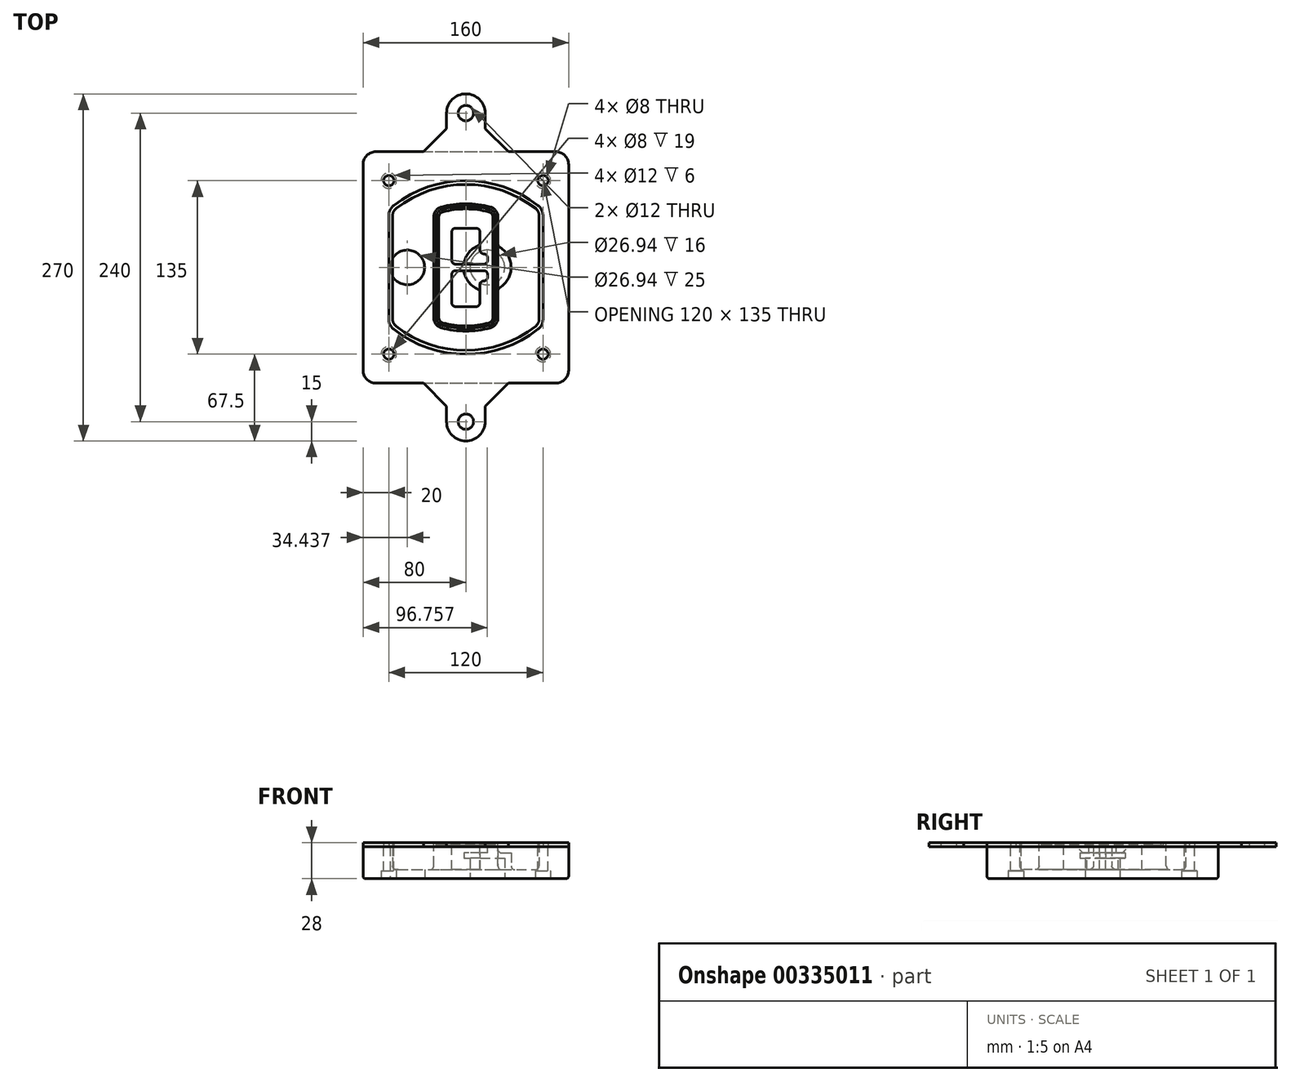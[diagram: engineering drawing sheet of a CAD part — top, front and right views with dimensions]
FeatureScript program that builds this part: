
annotation { "Feature Type Name" : "Feature", "Feature Type Description" : "" }
export const myFeature = defineFeature(function(context is Context, id is Id, definition is map)
    precondition{}
    {
        {
            var Q0;
            Q0=qCreatedBy(makeId("Top.planeOp"),FACE);
            var sketch = newSketch(context, id + "F0", { "sketchPlane" : qUnion([Q0])});
            skPoint(sketch, "E0.rect.middle", {"position": v(0, 0) * mm});
            skLineSegment(sketch, "E1.bottom", {"start": v(-70, -90) * mm, "end": v(70, -90) * mm});
            skLineSegment(sketch, "E1.top", {"start": v(-70, 90) * mm, "end": v(70, 90) * mm});
            skLineSegment(sketch, "E1.left", {"start": v(-80, -80) * mm, "end": v(-80, 80) * mm});
            skLineSegment(sketch, "E1.right", {"start": v(80, -80) * mm, "end": v(80, 80) * mm});
            skLineSegment(sketch, "E2", {"start": v(-80, 90) * mm, "end": v(80, -90) * mm, "construction": true});
            skLineSegment(sketch, "E3", {"start": v(80, 90) * mm, "end": v(-80, -90) * mm, "construction": true});
            skCircle(sketch, "E4", {"center": v(-60, 67.5) * mm, "radius": 4 * mm});
            skCircle(sketch, "E5", {"center": v(60, 67.5) * mm, "radius": 4 * mm});
            skCircle(sketch, "E6", {"center": v(60, -67.5) * mm, "radius": 4 * mm});
            skCircle(sketch, "E7", {"center": v(-60, -67.5) * mm, "radius": 4 * mm});
            skLineSegment(sketch, "E8", {"start": v(-60, 67.5) * mm, "end": v(60, 67.5) * mm, "construction": true});
            skLineSegment(sketch, "E9", {"start": v(60, 67.5) * mm, "end": v(60, -67.5) * mm, "construction": true});
            skLineSegment(sketch, "E10", {"start": v(60, -67.5) * mm, "end": v(-60, -67.5) * mm, "construction": true});
            skLineSegment(sketch, "E11", {"start": v(-60, -67.5) * mm, "end": v(-60, 67.5) * mm, "construction": true});
            skLineSegment(sketch, "E12", {"start": v(-60, 40.3) * mm, "end": v(-60, -40.3) * mm});
            skLineSegment(sketch, "E13", {"start": v(60, 40.3) * mm, "end": v(60, -40.3) * mm});
            skArc(sketch, "E14", {"start": v(56.15, 48.18) * mm, "mid": v(0, 67.5) * mm, "end": v(-56.15, 48.18) * mm});
            skArc(sketch, "E15", {"start": v(-56.15, -48.18) * mm, "mid": v(0, -67.5) * mm, "end": v(56.15, -48.18) * mm});
            skLineSegment(sketch, "E16", {"start": v(-60, 0) * mm, "end": v(60, 0) * mm, "construction": true});
            skPoint(sketch, "E17.visualSharp", {"position": v(-60, -45) * mm});
            skArc(sketch, "E17.filletArc", {"start": v(-60, -40.3) * mm, "mid": v(-58.99, -44.68) * mm, "end": v(-56.15, -48.18) * mm});
            skPoint(sketch, "E18.visualSharp", {"position": v(-60, 45) * mm});
            skArc(sketch, "E18.filletArc", {"start": v(-56.15, 48.18) * mm, "mid": v(-58.99, 44.68) * mm, "end": v(-60, 40.3) * mm});
            skPoint(sketch, "E19.visualSharp", {"position": v(60, 45) * mm});
            skArc(sketch, "E19.filletArc", {"start": v(60, 40.3) * mm, "mid": v(58.99, 44.68) * mm, "end": v(56.15, 48.18) * mm});
            skPoint(sketch, "E20.visualSharp", {"position": v(60, -45) * mm});
            skArc(sketch, "E20.filletArc", {"start": v(56.15, -48.18) * mm, "mid": v(58.99, -44.68) * mm, "end": v(60, -40.3) * mm});
            skPoint(sketch, "E21.visualSharp", {"position": v(-80, 90) * mm});
            skArc(sketch, "E21.filletArc", {"start": v(-70, 90) * mm, "mid": v(-77.07, 87.07) * mm, "end": v(-80, 80) * mm});
            skPoint(sketch, "E22.visualSharp", {"position": v(80, 90) * mm});
            skArc(sketch, "E22.filletArc", {"start": v(80, 80) * mm, "mid": v(77.07, 87.07) * mm, "end": v(70, 90) * mm});
            skPoint(sketch, "E23.visualSharp", {"position": v(80, -90) * mm});
            skArc(sketch, "E23.filletArc", {"start": v(70, -90) * mm, "mid": v(77.07, -87.07) * mm, "end": v(80, -80) * mm});
            skPoint(sketch, "E24.visualSharp", {"position": v(-80, -90) * mm});
            skArc(sketch, "E24.filletArc", {"start": v(-80, -80) * mm, "mid": v(-77.07, -87.07) * mm, "end": v(-70, -90) * mm});
            skArc(sketch, "E25.0", {"start": v(57, 40.3) * mm, "mid": v(56.3, 43.36) * mm, "end": v(54.3, 45.81) * mm});
            skLineSegment(sketch, "E25.1", {"start": v(57, 40.3) * mm, "end": v(57, -40.3) * mm});
            skArc(sketch, "E25.2", {"start": v(54.3, -45.81) * mm, "mid": v(56.3, -43.36) * mm, "end": v(57, -40.3) * mm});
            skArc(sketch, "E25.3", {"start": v(-54.3, -45.81) * mm, "mid": v(0, -64.5) * mm, "end": v(54.3, -45.81) * mm});
            skArc(sketch, "E25.4", {"start": v(-57, -40.3) * mm, "mid": v(-56.3, -43.36) * mm, "end": v(-54.3, -45.81) * mm});
            skArc(sketch, "E25.5", {"start": v(54.3, 45.81) * mm, "mid": v(0, 64.5) * mm, "end": v(-54.3, 45.81) * mm});
            skLineSegment(sketch, "E25.6", {"start": v(-57, 40.3) * mm, "end": v(-57, -40.3) * mm});
            skArc(sketch, "E25.7", {"start": v(-54.3, 45.81) * mm, "mid": v(-56.3, 43.36) * mm, "end": v(-57, 40.3) * mm});
            skArc(sketch, "E26.0", {"start": v(-58.62, 51.33) * mm, "mid": v(-62.58, 46.43) * mm, "end": v(-64, 40.3) * mm});
            skArc(sketch, "E26.1", {"start": v(58.62, 51.33) * mm, "mid": v(0, 71.5) * mm, "end": v(-58.62, 51.33) * mm});
            skArc(sketch, "E26.2", {"start": v(64, 40.3) * mm, "mid": v(62.58, 46.43) * mm, "end": v(58.62, 51.33) * mm});
            skLineSegment(sketch, "E26.3", {"start": v(64, 40.3) * mm, "end": v(64, -40.3) * mm});
            skArc(sketch, "E26.4", {"start": v(58.62, -51.33) * mm, "mid": v(62.58, -46.43) * mm, "end": v(64, -40.3) * mm});
            skLineSegment(sketch, "E26.5", {"start": v(-64, 40.3) * mm, "end": v(-64, -40.3) * mm});
            skArc(sketch, "E26.6", {"start": v(-58.62, -51.33) * mm, "mid": v(0, -71.5) * mm, "end": v(58.62, -51.33) * mm});
            skArc(sketch, "E26.7", {"start": v(-64, -40.3) * mm, "mid": v(-62.58, -46.43) * mm, "end": v(-58.62, -51.33) * mm});
            skSolve(sketch);
        }
        {
            var Q0;
            Q0=makeQuery(id+"F0.imprint","IMPRINT",FACE,{"disambiguationData":[TD([[makeQuery(id+"F0.imprint","IMPRINT",EDGE,{"derivedFrom":sQuery(id+"F0.wireOp",EDGE,"E1.bottom")}),1.0]])]});
            var Q1;
            Q1=makeQuery(id+"F0.imprint","IMPRINT",FACE,{"disambiguationData":[TD([[makeQuery(id+"F0.imprint","IMPRINT",EDGE,{"derivedFrom":sQuery(id+"F0.wireOp",EDGE,"E12")}),1.0]])]});
            var Q2;
            Q2=makeQuery(id+"F0.imprint","IMPRINT",FACE,{"disambiguationData":[TD([[makeQuery(id+"F0.imprint","IMPRINT",EDGE,{"derivedFrom":sQuery(id+"F0.wireOp",EDGE,"E25.0")}),1.0]])]});
            var Q3;
            Q3=makeQuery(id+"F0.imprint","IMPRINT",FACE,{"disambiguationData":[TD([[makeQuery(id+"F0.imprint","IMPRINT",EDGE,{"derivedFrom":sQuery(id+"F0.wireOp",EDGE,"E12")}),-1.0]])]});
            extrude(context, id + "F1", {"entities" : qUnion([Q0, Q1, Q2, Q3]), "oppositeDirection" : true, "depth" : 25 * mm});
        }
        {
            var Q0;
            Q0=makeQuery(id+"F0.imprint","IMPRINT",FACE,{"disambiguationData":[TD([[makeQuery(id+"F0.imprint","IMPRINT",EDGE,{"derivedFrom":sQuery(id+"F0.wireOp",EDGE,"E12")}),1.0]])]});
            extrude(context, id + "F2", {"entities" : qUnion([Q0]), "operationType" : NewBodyOperationType.ADD, "depth" : 3 * mm});
        }
        {
            var Q0;
            Q0=makeQuery(id+"F0.imprint","IMPRINT",FACE,{"disambiguationData":[TD([[makeQuery(id+"F0.imprint","IMPRINT",EDGE,{"derivedFrom":sQuery(id+"F0.wireOp",EDGE,"E25.0")}),1.0]])]});
            extrude(context, id + "F3", {"entities" : qUnion([Q0]), "operationType" : NewBodyOperationType.REMOVE, "oppositeDirection" : true, "depth" : 18 * mm});
        }
        {
            var Q0;
            Q0=makeQuery(id+"F2.opExtrude","CAP_FACE",FACE,{"disambiguationData":[OSD([sQuery(id+"F0.wireOp",EDGE,"E12"),sQuery(id+"F0.wireOp",EDGE,"E13"),sQuery(id+"F0.wireOp",EDGE,"E14"),sQuery(id+"F0.wireOp",EDGE,"E15"),sQuery(id+"F0.wireOp",EDGE,"E17.filletArc"),sQuery(id+"F0.wireOp",EDGE,"E18.filletArc"),sQuery(id+"F0.wireOp",EDGE,"E19.filletArc"),sQuery(id+"F0.wireOp",EDGE,"E20.filletArc"),sQuery(id+"F0.wireOp",EDGE,"E25.0"),sQuery(id+"F0.wireOp",EDGE,"E25.1"),sQuery(id+"F0.wireOp",EDGE,"E25.2"),sQuery(id+"F0.wireOp",EDGE,"E25.3"),sQuery(id+"F0.wireOp",EDGE,"E25.4"),sQuery(id+"F0.wireOp",EDGE,"E25.5"),sQuery(id+"F0.wireOp",EDGE,"E25.6"),sQuery(id+"F0.wireOp",EDGE,"E25.7")])],"isStart":false});
            var sketch = newSketch(context, id + "F4", { "sketchPlane" : qUnion([Q0])});
            skArc(sketch, "E27.0", {"start": v(-19.08, -46.97) * mm, "mid": v(0, -49.5) * mm, "end": v(19.08, -46.97) * mm});
            skArc(sketch, "E28.0", {"start": v(19.08, 46.97) * mm, "mid": v(0, 49.5) * mm, "end": v(-19.08, 46.97) * mm});
            skLineSegment(sketch, "E29", {"start": v(-25, 39.25) * mm, "end": v(-25, -39.25) * mm});
            skLineSegment(sketch, "E30", {"start": v(25, 39.25) * mm, "end": v(25, -39.25) * mm});
            skLineSegment(sketch, "E31", {"start": v(-25, 45.1) * mm, "end": v(25, 45.1) * mm, "construction": true});
            skLineSegment(sketch, "E32", {"start": v(-25, -45.1) * mm, "end": v(25, -45.1) * mm, "construction": true});
            skPoint(sketch, "E33.visualSharp", {"position": v(-25, 45.1) * mm});
            skArc(sketch, "E33.filletArc", {"start": v(-19.08, 46.97) * mm, "mid": v(-23.35, 44.11) * mm, "end": v(-25, 39.25) * mm});
            skPoint(sketch, "E34.visualSharp", {"position": v(25, 45.1) * mm});
            skArc(sketch, "E34.filletArc", {"start": v(25, 39.25) * mm, "mid": v(23.35, 44.11) * mm, "end": v(19.08, 46.97) * mm});
            skPoint(sketch, "E35.visualSharp", {"position": v(25, -45.1) * mm});
            skArc(sketch, "E35.filletArc", {"start": v(19.08, -46.97) * mm, "mid": v(23.35, -44.11) * mm, "end": v(25, -39.25) * mm});
            skPoint(sketch, "E36.visualSharp", {"position": v(-25, -45.1) * mm});
            skArc(sketch, "E36.filletArc", {"start": v(-25, -39.25) * mm, "mid": v(-23.35, -44.11) * mm, "end": v(-19.08, -46.97) * mm});
            skArc(sketch, "E37.0", {"start": v(54.3, 45.81) * mm, "mid": v(0, 64.5) * mm, "end": v(-54.3, 45.81) * mm});
            skArc(sketch, "E37.1", {"start": v(-54.3, 45.81) * mm, "mid": v(-56.3, 43.36) * mm, "end": v(-57, 40.3) * mm});
            skLineSegment(sketch, "E37.2", {"start": v(-57, 40.3) * mm, "end": v(-57, -40.3) * mm});
            skArc(sketch, "E37.3", {"start": v(-57, -40.3) * mm, "mid": v(-56.3, -43.36) * mm, "end": v(-54.3, -45.81) * mm});
            skArc(sketch, "E37.4", {"start": v(-54.3, -45.81) * mm, "mid": v(0, -64.5) * mm, "end": v(54.3, -45.81) * mm});
            skArc(sketch, "E37.5", {"start": v(54.3, -45.81) * mm, "mid": v(56.3, -43.36) * mm, "end": v(57, -40.3) * mm});
            skLineSegment(sketch, "E37.6", {"start": v(57, 40.3) * mm, "end": v(57, -40.3) * mm});
            skArc(sketch, "E37.7", {"start": v(57, 40.3) * mm, "mid": v(56.3, 43.36) * mm, "end": v(54.3, 45.81) * mm});
            skLineSegment(sketch, "E38.0", {"start": v(23, 39.25) * mm, "end": v(23, -39.25) * mm});
            skArc(sketch, "E38.1", {"start": v(18.56, -45.04) * mm, "mid": v(21.76, -42.9) * mm, "end": v(23, -39.25) * mm});
            skArc(sketch, "E38.2", {"start": v(-18.56, -45.04) * mm, "mid": v(0, -47.5) * mm, "end": v(18.56, -45.04) * mm});
            skArc(sketch, "E38.3", {"start": v(-23, -39.25) * mm, "mid": v(-21.76, -42.9) * mm, "end": v(-18.56, -45.04) * mm});
            skLineSegment(sketch, "E38.4", {"start": v(-23, 39.25) * mm, "end": v(-23, -39.25) * mm});
            skArc(sketch, "E38.5", {"start": v(23, 39.25) * mm, "mid": v(21.76, 42.9) * mm, "end": v(18.56, 45.04) * mm});
            skArc(sketch, "E38.6", {"start": v(-18.56, 45.04) * mm, "mid": v(-21.76, 42.9) * mm, "end": v(-23, 39.25) * mm});
            skArc(sketch, "E38.7", {"start": v(18.56, 45.04) * mm, "mid": v(0, 47.5) * mm, "end": v(-18.56, 45.04) * mm});
            skArc(sketch, "E39.0", {"start": v(21, 39.25) * mm, "mid": v(20.18, 41.68) * mm, "end": v(18.04, 43.1) * mm});
            skLineSegment(sketch, "E39.1", {"start": v(21, 39.25) * mm, "end": v(21, -39.25) * mm});
            skArc(sketch, "E39.2", {"start": v(18.04, -43.1) * mm, "mid": v(20.18, -41.68) * mm, "end": v(21, -39.25) * mm});
            skArc(sketch, "E39.3", {"start": v(-18.04, -43.1) * mm, "mid": v(0, -45.5) * mm, "end": v(18.04, -43.1) * mm});
            skArc(sketch, "E39.4", {"start": v(-21, -39.25) * mm, "mid": v(-20.18, -41.68) * mm, "end": v(-18.04, -43.1) * mm});
            skArc(sketch, "E39.5", {"start": v(18.04, 43.1) * mm, "mid": v(0, 45.5) * mm, "end": v(-18.04, 43.1) * mm});
            skLineSegment(sketch, "E39.6", {"start": v(-21, 39.25) * mm, "end": v(-21, -39.25) * mm});
            skArc(sketch, "E39.7", {"start": v(-18.04, 43.1) * mm, "mid": v(-20.18, 41.68) * mm, "end": v(-21, 39.25) * mm});
            skLineSegment(sketch, "E40", {"start": v(-25, 0) * mm, "end": v(25, 0) * mm, "construction": true});
            skLineSegment(sketch, "E41", {"start": v(-11, 5.5) * mm, "end": v(-11, 27.5) * mm});
            skLineSegment(sketch, "E42", {"start": v(-8, 30.5) * mm, "end": v(8, 30.5) * mm});
            skLineSegment(sketch, "E43", {"start": v(11, 27.5) * mm, "end": v(11, 13.5) * mm});
            skLineSegment(sketch, "E44", {"start": v(14, 10.5) * mm, "end": v(14, 10.5) * mm});
            skLineSegment(sketch, "E45", {"start": v(17, 7.5) * mm, "end": v(17, 5.5) * mm});
            skLineSegment(sketch, "E46", {"start": v(14, 2.5) * mm, "end": v(-8, 2.5) * mm});
            skPoint(sketch, "E47.visualSharp", {"position": v(-11, 30.5) * mm});
            skArc(sketch, "E47.filletArc", {"start": v(-8, 30.5) * mm, "mid": v(-10.12, 29.62) * mm, "end": v(-11, 27.5) * mm});
            skPoint(sketch, "E48.visualSharp", {"position": v(11, 30.5) * mm});
            skArc(sketch, "E48.filletArc", {"start": v(11, 27.5) * mm, "mid": v(10.12, 29.62) * mm, "end": v(8, 30.5) * mm});
            skPoint(sketch, "E49.visualSharp", {"position": v(11, 10.5) * mm});
            skArc(sketch, "E49.filletArc", {"start": v(11, 13.5) * mm, "mid": v(11.88, 11.38) * mm, "end": v(14, 10.5) * mm});
            skPoint(sketch, "E50.visualSharp", {"position": v(17, 10.5) * mm});
            skArc(sketch, "E50.filletArc", {"start": v(17, 7.5) * mm, "mid": v(16.12, 9.62) * mm, "end": v(14, 10.5) * mm});
            skPoint(sketch, "E51.visualSharp", {"position": v(17, 2.5) * mm});
            skArc(sketch, "E51.filletArc", {"start": v(14, 2.5) * mm, "mid": v(16.12, 3.38) * mm, "end": v(17, 5.5) * mm});
            skPoint(sketch, "E52.visualSharp", {"position": v(-11, 2.5) * mm});
            skArc(sketch, "E52.filletArc", {"start": v(-11, 5.5) * mm, "mid": v(-10.12, 3.38) * mm, "end": v(-8, 2.5) * mm});
            skLineSegment(sketch, "E53.0.MirrorCS", {"start": v(14, -2.5) * mm, "end": v(-8, -2.5) * mm});
            skArc(sketch, "E54.0.MirrorCS", {"start": v(-11, -5.5) * mm, "mid": v(-10.12, -3.38) * mm, "end": v(-8, -2.5) * mm});
            skLineSegment(sketch, "E55.0.MirrorCS", {"start": v(-11, -5.5) * mm, "end": v(-11, -27.5) * mm});
            skArc(sketch, "E56.0.MirrorCS", {"start": v(-8, -30.5) * mm, "mid": v(-10.12, -29.62) * mm, "end": v(-11, -27.5) * mm});
            skLineSegment(sketch, "E57.0.MirrorCS", {"start": v(-8, -30.5) * mm, "end": v(8, -30.5) * mm});
            skArc(sketch, "E58.0.MirrorCS", {"start": v(11, -27.5) * mm, "mid": v(10.12, -29.62) * mm, "end": v(8, -30.5) * mm});
            skLineSegment(sketch, "E59.0.MirrorCS", {"start": v(11, -27.5) * mm, "end": v(11, -13.5) * mm});
            skArc(sketch, "E60.0.MirrorCS", {"start": v(11, -13.5) * mm, "mid": v(11.88, -11.38) * mm, "end": v(14, -10.5) * mm});
            skArc(sketch, "E61.0.MirrorCS", {"start": v(17, -7.5) * mm, "mid": v(16.12, -9.62) * mm, "end": v(14, -10.5) * mm});
            skLineSegment(sketch, "E62.0.MirrorCS", {"start": v(17, -7.5) * mm, "end": v(17, -5.5) * mm});
            skArc(sketch, "E63.0.MirrorCS", {"start": v(14, -2.5) * mm, "mid": v(16.12, -3.38) * mm, "end": v(17, -5.5) * mm});
            skSolve(sketch);
        }
        {
            var Q0;
            Q0=makeQuery(id+"F4.imprint","IMPRINT",FACE,{"disambiguationData":[TD([[makeQuery(id+"F4.imprint","IMPRINT",EDGE,{"derivedFrom":sQuery(id+"F4.wireOp",EDGE,"E27.0")}),1.0]])]});
            var Q1;
            Q1=makeQuery(id+"F4.imprint","IMPRINT",FACE,{"disambiguationData":[TD([[makeQuery(id+"F4.imprint","IMPRINT",EDGE,{"derivedFrom":sQuery(id+"F4.wireOp",EDGE,"E38.0")}),-1.0]])]});
            var Q2;
            Q2=makeQuery(id+"F4.imprint","IMPRINT",FACE,{"disambiguationData":[TD([[makeQuery(id+"F4.imprint","IMPRINT",EDGE,{"derivedFrom":sQuery(id+"F4.wireOp",EDGE,"E39.0")}),1.0]])]});
            extrude(context, id + "F5", {"entities" : qUnion([Q0, Q1, Q2]), "operationType" : NewBodyOperationType.ADD, "endBound" : BoundingType.UP_TO_NEXT, "oppositeDirection" : true, "depth" : 25 * mm});
        }
        {
            var Q0;
            Q0=makeQuery(id+"F4.imprint","IMPRINT",FACE,{"disambiguationData":[TD([[makeQuery(id+"F4.imprint","IMPRINT",EDGE,{"derivedFrom":sQuery(id+"F4.wireOp",EDGE,"E38.0")}),-1.0]])]});
            extrude(context, id + "F6", {"entities" : qUnion([Q0]), "operationType" : NewBodyOperationType.REMOVE, "oppositeDirection" : true, "depth" : 2 * mm});
        }
        {
            var Q0;
            Q0=makeQuery(id+"F1.opExtrude","CAP_FACE",FACE,{"disambiguationData":[OSD([sQuery(id+"F0.wireOp",EDGE,"E1.bottom"),sQuery(id+"F0.wireOp",EDGE,"E1.top"),sQuery(id+"F0.wireOp",EDGE,"E1.left"),sQuery(id+"F0.wireOp",EDGE,"E1.right"),sQuery(id+"F0.wireOp",EDGE,"E4"),sQuery(id+"F0.wireOp",EDGE,"E5"),sQuery(id+"F0.wireOp",EDGE,"E6"),sQuery(id+"F0.wireOp",EDGE,"E7"),sQuery(id+"F0.wireOp",EDGE,"E21.filletArc"),sQuery(id+"F0.wireOp",EDGE,"E22.filletArc"),sQuery(id+"F0.wireOp",EDGE,"E23.filletArc"),sQuery(id+"F0.wireOp",EDGE,"E24.filletArc")])],"isStart":false});
            var sketch = newSketch(context, id + "F7", { "sketchPlane" : qUnion([Q0])});
            skCircle(sketch, "E64", {"center": v(16.76, 0) * mm, "radius": 13.47 * mm});
            skCircle(sketch, "E65", {"center": v(-45.56, 0) * mm, "radius": 13.47 * mm});
            skLineSegment(sketch, "E66", {"start": v(80, 0) * mm, "end": v(-80, 0) * mm});
            skCircle(sketch, "E67", {"center": v(16.76, 0) * mm, "radius": 18.47 * mm});
            skCircle(sketch, "E68", {"center": v(60, -67.5) * mm, "radius": 6 * mm});
            skCircle(sketch, "E69", {"center": v(-60, -67.5) * mm, "radius": 6 * mm});
            skCircle(sketch, "E70", {"center": v(-60, 67.5) * mm, "radius": 6 * mm});
            skCircle(sketch, "E71", {"center": v(60, 67.5) * mm, "radius": 6 * mm});
            skSolve(sketch);
        }
        {
            var Q0;
            {var subQ1=sQuery(id+"F7.wireOp",EDGE,"E66");var subQ4=sQuery(id+"F7.wireOp",EDGE,"E64");var subQ6=makeQuery(id+"F7.imprint","INTERSECT",VERTEX,{"disambiguationData":[OD(0.0)],"derivedFrom":[subQ4,subQ1]});Q0=makeQuery(id+"F7.imprint","IMPRINT",FACE,{"disambiguationData":[TD([[makeQuery(id+"F7.imprint","IMPRINT",EDGE,{"disambiguationData":[TD([[subQ6,-1.0]])],"derivedFrom":subQ4}),-1.0]])]});}
            var Q1;
            {var subQ0=sQuery(id+"F7.wireOp",EDGE,"E66");var subQ1=sQuery(id+"F7.wireOp",EDGE,"E64");var subQ3=makeQuery(id+"F7.imprint","INTERSECT",VERTEX,{"disambiguationData":[OD(0.0)],"derivedFrom":[subQ1,subQ0]});Q1=makeQuery(id+"F7.imprint","IMPRINT",FACE,{"disambiguationData":[TD([[makeQuery(id+"F7.imprint","IMPRINT",EDGE,{"disambiguationData":[TD([[subQ3,-1.0]])],"derivedFrom":subQ1}),1.0]])]});}
            var Q2;
            {var subQ0=sQuery(id+"F7.wireOp",EDGE,"E66");var subQ1=sQuery(id+"F7.wireOp",EDGE,"E64");var subQ3=makeQuery(id+"F7.imprint","INTERSECT",VERTEX,{"disambiguationData":[OD(0.0)],"derivedFrom":[subQ1,subQ0]});Q2=makeQuery(id+"F7.imprint","IMPRINT",FACE,{"disambiguationData":[TD([[makeQuery(id+"F7.imprint","IMPRINT",EDGE,{"disambiguationData":[TD([[subQ3,1.0]])],"derivedFrom":subQ1}),1.0]])]});}
            var Q3;
            {var subQ1=sQuery(id+"F7.wireOp",EDGE,"E66");var subQ4=sQuery(id+"F7.wireOp",EDGE,"E64");var subQ6=makeQuery(id+"F7.imprint","INTERSECT",VERTEX,{"disambiguationData":[OD(0.0)],"derivedFrom":[subQ4,subQ1]});Q3=makeQuery(id+"F7.imprint","IMPRINT",FACE,{"disambiguationData":[TD([[makeQuery(id+"F7.imprint","IMPRINT",EDGE,{"disambiguationData":[TD([[subQ6,1.0]])],"derivedFrom":subQ4}),-1.0]])]});}
            extrude(context, id + "F8", {"entities" : qUnion([Q0, Q1, Q2, Q3]), "operationType" : NewBodyOperationType.ADD, "oppositeDirection" : true, "depth" : 20 * mm});
        }
        {
            var Q0;
            {var subQ0=sQuery(id+"F7.wireOp",EDGE,"E66");var subQ1=sQuery(id+"F7.wireOp",EDGE,"E64");var subQ3=makeQuery(id+"F7.imprint","INTERSECT",VERTEX,{"disambiguationData":[OD(0.0)],"derivedFrom":[subQ1,subQ0]});Q0=makeQuery(id+"F7.imprint","IMPRINT",FACE,{"disambiguationData":[TD([[makeQuery(id+"F7.imprint","IMPRINT",EDGE,{"disambiguationData":[TD([[subQ3,-1.0]])],"derivedFrom":subQ1}),1.0]])]});}
            var Q1;
            {var subQ0=sQuery(id+"F7.wireOp",EDGE,"E66");var subQ1=sQuery(id+"F7.wireOp",EDGE,"E64");var subQ3=makeQuery(id+"F7.imprint","INTERSECT",VERTEX,{"disambiguationData":[OD(0.0)],"derivedFrom":[subQ1,subQ0]});Q1=makeQuery(id+"F7.imprint","IMPRINT",FACE,{"disambiguationData":[TD([[makeQuery(id+"F7.imprint","IMPRINT",EDGE,{"disambiguationData":[TD([[subQ3,1.0]])],"derivedFrom":subQ1}),1.0]])]});}
            extrude(context, id + "F9", {"entities" : qUnion([Q0, Q1]), "operationType" : NewBodyOperationType.REMOVE, "oppositeDirection" : true, "depth" : 16 * mm});
        }
        {
            var Q0;
            {var subQ0=sQuery(id+"F7.wireOp",EDGE,"E66");var subQ1=sQuery(id+"F7.wireOp",EDGE,"E65");var subQ3=makeQuery(id+"F7.imprint","INTERSECT",VERTEX,{"disambiguationData":[OD(0.0)],"derivedFrom":[subQ1,subQ0]});Q0=makeQuery(id+"F7.imprint","IMPRINT",FACE,{"disambiguationData":[TD([[makeQuery(id+"F7.imprint","IMPRINT",EDGE,{"disambiguationData":[TD([[subQ3,-1.0]])],"derivedFrom":subQ1}),1.0]])]});}
            var Q1;
            {var subQ0=sQuery(id+"F7.wireOp",EDGE,"E66");var subQ1=sQuery(id+"F7.wireOp",EDGE,"E65");var subQ3=makeQuery(id+"F7.imprint","INTERSECT",VERTEX,{"disambiguationData":[OD(0.0)],"derivedFrom":[subQ1,subQ0]});Q1=makeQuery(id+"F7.imprint","IMPRINT",FACE,{"disambiguationData":[TD([[makeQuery(id+"F7.imprint","IMPRINT",EDGE,{"disambiguationData":[TD([[subQ3,1.0]])],"derivedFrom":subQ1}),1.0]])]});}
            extrude(context, id + "F10", {"entities" : qUnion([Q0, Q1]), "operationType" : NewBodyOperationType.REMOVE, "oppositeDirection" : true, "depth" : 25 * mm});
        }
        {
            var Q0;
            Q0=makeQuery(id+"F7.imprint","IMPRINT",FACE,{"disambiguationData":[TD([[makeQuery(id+"F7.imprint","IMPRINT",EDGE,{"derivedFrom":sQuery(id+"F7.wireOp",EDGE,"E68")}),1.0]])]});
            var Q1;
            Q1=makeQuery(id+"F7.imprint","IMPRINT",FACE,{"disambiguationData":[TD([[makeQuery(id+"F7.imprint","IMPRINT",EDGE,{"derivedFrom":makeQuery(id+"F1.opExtrude","CAP_EDGE",EDGE,{"disambiguationData":[OSD([sQuery(id+"F0.wireOp",EDGE,"E5")])],"isStart":false})}),-1.0]])]});
            var Q2;
            Q2=makeQuery(id+"F7.imprint","IMPRINT",FACE,{"disambiguationData":[TD([[makeQuery(id+"F7.imprint","IMPRINT",EDGE,{"derivedFrom":sQuery(id+"F7.wireOp",EDGE,"E69")}),1.0]])]});
            var Q3;
            Q3=makeQuery(id+"F7.imprint","IMPRINT",FACE,{"disambiguationData":[TD([[makeQuery(id+"F7.imprint","IMPRINT",EDGE,{"derivedFrom":makeQuery(id+"F1.opExtrude","CAP_EDGE",EDGE,{"disambiguationData":[OSD([sQuery(id+"F0.wireOp",EDGE,"E4")])],"isStart":false})}),-1.0]])]});
            var Q4;
            Q4=makeQuery(id+"F7.imprint","IMPRINT",FACE,{"disambiguationData":[TD([[makeQuery(id+"F7.imprint","IMPRINT",EDGE,{"derivedFrom":sQuery(id+"F7.wireOp",EDGE,"E70")}),1.0]])]});
            var Q5;
            Q5=makeQuery(id+"F7.imprint","IMPRINT",FACE,{"disambiguationData":[TD([[makeQuery(id+"F7.imprint","IMPRINT",EDGE,{"derivedFrom":makeQuery(id+"F1.opExtrude","CAP_EDGE",EDGE,{"disambiguationData":[OSD([sQuery(id+"F0.wireOp",EDGE,"E7")])],"isStart":false})}),-1.0]])]});
            var Q6;
            Q6=makeQuery(id+"F7.imprint","IMPRINT",FACE,{"disambiguationData":[TD([[makeQuery(id+"F7.imprint","IMPRINT",EDGE,{"derivedFrom":sQuery(id+"F7.wireOp",EDGE,"E71")}),1.0]])]});
            var Q7;
            Q7=makeQuery(id+"F7.imprint","IMPRINT",FACE,{"disambiguationData":[TD([[makeQuery(id+"F7.imprint","IMPRINT",EDGE,{"derivedFrom":makeQuery(id+"F1.opExtrude","CAP_EDGE",EDGE,{"disambiguationData":[OSD([sQuery(id+"F0.wireOp",EDGE,"E6")])],"isStart":false})}),-1.0]])]});
            extrude(context, id + "F11", {"entities" : qUnion([Q0, Q1, Q2, Q3, Q4, Q5, Q6, Q7]), "operationType" : NewBodyOperationType.REMOVE, "oppositeDirection" : true, "depth" : 6 * mm});
        }
        {
            var Q0;
            Q0=makeQuery(id+"F9.boolean.opBoolean","COPY",FACE,{"derivedFrom":makeQuery(id+"F9.opExtrude","CAP_FACE",FACE,{"disambiguationData":[OSD([sQuery(id+"F7.wireOp",EDGE,"E64")])],"isStart":false})});
            var sketch = newSketch(context, id + "F12", { "sketchPlane" : qUnion([Q0])});
            skArc(sketch, "E72.0", {"start": v(11, 17.55) * mm, "mid": v(2.57, 11.82) * mm, "end": v(-1.54, 2.5) * mm});
            skArc(sketch, "E72.1", {"start": v(-1.54, -2.5) * mm, "mid": v(2.57, -11.82) * mm, "end": v(11, -17.55) * mm});
            skLineSegment(sketch, "E73", {"start": v(-1.54, -2.5) * mm, "end": v(14, -2.5) * mm});
            skLineSegment(sketch, "E74.0", {"start": v(14, 2.5) * mm, "end": v(-1.54, 2.5) * mm});
            skArc(sketch, "E74.1", {"start": v(14, 2.5) * mm, "mid": v(16.12, 3.38) * mm, "end": v(17, 5.5) * mm});
            skLineSegment(sketch, "E74.2", {"start": v(17, 7.5) * mm, "end": v(17, 5.5) * mm});
            skArc(sketch, "E74.3", {"start": v(17, 7.5) * mm, "mid": v(16.12, 9.62) * mm, "end": v(14, 10.5) * mm});
            skArc(sketch, "E74.4", {"start": v(11, 13.5) * mm, "mid": v(11.88, 11.38) * mm, "end": v(14, 10.5) * mm});
            skLineSegment(sketch, "E74.5", {"start": v(11, 17.55) * mm, "end": v(11, 13.5) * mm});
            skLineSegment(sketch, "E74.7", {"start": v(14, -2.5) * mm, "end": v(-1.54, -2.5) * mm});
            skArc(sketch, "E74.8", {"start": v(14, -2.5) * mm, "mid": v(16.12, -3.38) * mm, "end": v(17, -5.5) * mm});
            skLineSegment(sketch, "E74.9", {"start": v(17, -7.5) * mm, "end": v(17, -5.5) * mm});
            skArc(sketch, "E74.10", {"start": v(17, -7.5) * mm, "mid": v(16.12, -9.62) * mm, "end": v(14, -10.5) * mm});
            skArc(sketch, "E74.11", {"start": v(11, -13.5) * mm, "mid": v(11.88, -11.38) * mm, "end": v(14, -10.5) * mm});
            skLineSegment(sketch, "E74.12", {"start": v(11, -17.55) * mm, "end": v(11, -13.5) * mm});
            skPoint(sketch, "E75.orphan", {"position": v(11, -27.5) * mm});
            skPoint(sketch, "E76.orphan", {"position": v(-8, -2.5) * mm});
            skPoint(sketch, "E77.orphan", {"position": v(-8, 2.5) * mm});
            skPoint(sketch, "E78.orphan", {"position": v(11, 27.5) * mm});
            skSolve(sketch);
        }
        {
            var Q0;
            {var subQ7=sQuery(id+"F12.wireOp",EDGE,"E72.0");var subQ14=sQuery(id+"F12.wireOp",EDGE,"E72.1");var subQ16=sQuery(id+"F12.wireOp",EDGE,"E74.1");var subQ18=sQuery(id+"F12.wireOp",EDGE,"E74.8");Q0=qUnion([makeQuery(id+"F12.imprint","IMPRINT",FACE,{"disambiguationData":[TD([[makeQuery(id+"F12.imprint","IMPRINT",EDGE,{"derivedFrom":subQ7}),1.0]])]}),makeQuery(id+"F12.imprint","IMPRINT",FACE,{"disambiguationData":[TD([[makeQuery(id+"F12.imprint","IMPRINT",EDGE,{"derivedFrom":subQ14}),1.0]])]}),makeQuery(id+"F12.imprint","IMPRINT",FACE,{"disambiguationData":[TD([[makeQuery(id+"F12.imprint","IMPRINT",EDGE,{"derivedFrom":subQ16}),1.0]])]}),makeQuery(id+"F12.imprint","IMPRINT",FACE,{"disambiguationData":[TD([[makeQuery(id+"F12.imprint","IMPRINT",EDGE,{"derivedFrom":subQ18}),-1.0]])]})]);}
            var Q1;
            Q1=makeQuery(id+"F5.boolean.opBoolean","SPLIT",FACE,{"disambiguationData":[TD([makeQuery(id+"F5.opExtrude","SWEPT_FACE",FACE,{"disambiguationData":[OSD([sQuery(id+"F4.wireOp",EDGE,"E41")])]})])],"derivedFrom":makeQuery(id+"F3.boolean.opBoolean","COPY",FACE,{"derivedFrom":makeQuery(id+"F3.opExtrude","CAP_FACE",FACE,{"disambiguationData":[OSD([sQuery(id+"F0.wireOp",EDGE,"E25.0"),sQuery(id+"F0.wireOp",EDGE,"E25.1"),sQuery(id+"F0.wireOp",EDGE,"E25.2"),sQuery(id+"F0.wireOp",EDGE,"E25.3"),sQuery(id+"F0.wireOp",EDGE,"E25.4"),sQuery(id+"F0.wireOp",EDGE,"E25.5"),sQuery(id+"F0.wireOp",EDGE,"E25.6"),sQuery(id+"F0.wireOp",EDGE,"E25.7")])],"isStart":false})})});
            extrude(context, id + "F13", {"entities" : qUnion([Q0]), "operationType" : NewBodyOperationType.REMOVE, "endBound" : BoundingType.UP_TO_SURFACE, "endBoundEntityFace" : qUnion([Q1]), "depth" : 25 * mm});
        }
        {
            var Q0;
            Q0=makeQuery(id+"F3.boolean.opBoolean","COPY",EDGE,{"derivedFrom":makeQuery(id+"F3.opExtrude","CAP_EDGE",EDGE,{"disambiguationData":[OSD([sQuery(id+"F0.wireOp",EDGE,"E25.6")])],"isStart":false})});
            var Q1;
            Q1=makeQuery(id+"F8.boolean.opBoolean","INTERSECT",EDGE,{"derivedFrom":[makeQuery(id+"F5.opExtrude","SWEPT_FACE",FACE,{"disambiguationData":[OSD([sQuery(id+"F4.wireOp",EDGE,"E30")])]}),makeQuery(id+"F8.opExtrude","CAP_FACE",FACE,{"disambiguationData":[OSD([sQuery(id+"F7.wireOp",EDGE,"E67")])],"isStart":false})]});
            var Q2;
            Q2=makeQuery(id+"F8.boolean.opBoolean","INTERSECT",EDGE,{"disambiguationData":[OD(1.0)],"derivedFrom":[makeQuery(id+"F5.opExtrude","SWEPT_FACE",FACE,{"disambiguationData":[OSD([sQuery(id+"F4.wireOp",EDGE,"E30")])]}),makeQuery(id+"F8.opExtrude","SWEPT_FACE",FACE,{"disambiguationData":[OSD([sQuery(id+"F7.wireOp",EDGE,"E67")])]})]});
            var Q3;
            {var subQ0=sQuery(id+"F4.wireOp",EDGE,"E30");Q3=makeQuery(id+"F8.boolean.opBoolean","SPLIT",EDGE,{"disambiguationData":[TD([makeQuery(id+"F5.opExtrude","SWEPT_FACE",FACE,{"disambiguationData":[OSD([sQuery(id+"F4.wireOp",EDGE,"E35.filletArc")])]})])],"derivedFrom":makeQuery(id+"F5.opExtrude","CAP_EDGE",EDGE,{"disambiguationData":[OSD([subQ0])],"isStart":false})});}
            var Q4;
            {var subQ0=sQuery(id+"F0.wireOp",EDGE,"E25.7");var subQ1=sQuery(id+"F0.wireOp",EDGE,"E25.1");var subQ2=sQuery(id+"F0.wireOp",EDGE,"E25.6");var subQ3=sQuery(id+"F0.wireOp",EDGE,"E25.5");var subQ4=sQuery(id+"F0.wireOp",EDGE,"E25.4");var subQ5=sQuery(id+"F0.wireOp",EDGE,"E25.0");var subQ6=sQuery(id+"F0.wireOp",EDGE,"E25.2");var subQ7=sQuery(id+"F0.wireOp",EDGE,"E25.3");Q4=makeQuery(id+"F8.boolean.opBoolean","INTERSECT",EDGE,{"derivedFrom":[makeQuery(id+"F5.boolean.opBoolean","SPLIT",FACE,{"disambiguationData":[TD([makeQuery(id+"F2.opExtrude","SWEPT_FACE",FACE,{"disambiguationData":[OSD([subQ5])]})])],"derivedFrom":makeQuery(id+"F3.boolean.opBoolean","COPY",FACE,{"derivedFrom":makeQuery(id+"F3.opExtrude","CAP_FACE",FACE,{"disambiguationData":[OSD([subQ5,subQ1,subQ6,subQ7,subQ4,subQ3,subQ2,subQ0])],"isStart":false})})}),makeQuery(id+"F8.opExtrude","SWEPT_FACE",FACE,{"disambiguationData":[OSD([sQuery(id+"F7.wireOp",EDGE,"E67")])]})]});}
            var Q5;
            Q5=makeQuery(id+"F8.boolean.opBoolean","INTERSECT",EDGE,{"disambiguationData":[OD(0.0)],"derivedFrom":[makeQuery(id+"F5.opExtrude","SWEPT_FACE",FACE,{"disambiguationData":[OSD([sQuery(id+"F4.wireOp",EDGE,"E30")])]}),makeQuery(id+"F8.opExtrude","SWEPT_FACE",FACE,{"disambiguationData":[OSD([sQuery(id+"F7.wireOp",EDGE,"E67")])]})]});
            fillet(context, id + "F14", {"entities" : qUnion([Q0, Q1, Q2, Q3, Q4, Q5]), "radius" : 3 * mm, "tangentPropagation" : true, "allowEdgeOverflow" : false});
        }
        {
            var Q0;
            Q0=makeQuery(id+"F1.opExtrude","CAP_EDGE",EDGE,{"disambiguationData":[OSD([sQuery(id+"F0.wireOp",EDGE,"E1.bottom")])],"isStart":false});
            fillet(context, id + "F15", {"entities" : qUnion([Q0]), "radius" : 2 * mm, "tangentPropagation" : true, "allowEdgeOverflow" : false});
        }
        {
            var Q0;
            {var subQ0=sQuery(id+"F0.wireOp",EDGE,"E21.filletArc");var subQ1=sQuery(id+"F0.wireOp",EDGE,"E7");var subQ2=sQuery(id+"F0.wireOp",EDGE,"E6");var subQ3=sQuery(id+"F0.wireOp",EDGE,"E5");var subQ4=sQuery(id+"F0.wireOp",EDGE,"E4");var subQ5=sQuery(id+"F0.wireOp",EDGE,"E22.filletArc");var subQ6=sQuery(id+"F0.wireOp",EDGE,"E1.bottom");var subQ7=sQuery(id+"F0.wireOp",EDGE,"E1.right");var subQ8=sQuery(id+"F0.wireOp",EDGE,"E1.top");var subQ9=sQuery(id+"F0.wireOp",EDGE,"E1.left");var subQ10=sQuery(id+"F0.wireOp",EDGE,"E23.filletArc");var subQ11=sQuery(id+"F0.wireOp",EDGE,"E24.filletArc");Q0=makeQuery(id+"F2.boolean.opBoolean","SPLIT",FACE,{"disambiguationData":[TD([makeQuery(id+"F1.opExtrude","SWEPT_FACE",FACE,{"disambiguationData":[OSD([subQ6])]})])],"derivedFrom":makeQuery(id+"F1.opExtrude","CAP_FACE",FACE,{"disambiguationData":[OSD([subQ6,subQ8,subQ9,subQ7,subQ4,subQ3,subQ2,subQ1,subQ0,subQ5,subQ10,subQ11])],"isStart":true})});}
            var sketch = newSketch(context, id + "F16", { "sketchPlane" : qUnion([Q0])});
            skLineSegment(sketch, "E79.0", {"start": v(-70, 90) * mm, "end": v(-33, 90) * mm});
            skLineSegment(sketch, "E79.1", {"start": v(-80, -80) * mm, "end": v(-80, 80) * mm});
            skArc(sketch, "E79.2", {"start": v(-70, 90) * mm, "mid": v(-77.07, 87.07) * mm, "end": v(-80, 80) * mm});
            skArc(sketch, "E79.3", {"start": v(-80, -80) * mm, "mid": v(-77.07, -87.07) * mm, "end": v(-70, -90) * mm});
            skLineSegment(sketch, "E79.4", {"start": v(-70, -90) * mm, "end": v(-33, -90) * mm});
            skArc(sketch, "E79.5", {"start": v(70, -90) * mm, "mid": v(77.07, -87.07) * mm, "end": v(80, -80) * mm});
            skLineSegment(sketch, "E79.6", {"start": v(80, -80) * mm, "end": v(80, 80) * mm});
            skArc(sketch, "E79.7", {"start": v(80, 80) * mm, "mid": v(77.07, 87.07) * mm, "end": v(70, 90) * mm});
            skLineSegment(sketch, "E79.8", {"start": v(60, 40.3) * mm, "end": v(60, -40.3) * mm});
            skArc(sketch, "E79.9", {"start": v(56.15, 48.18) * mm, "mid": v(0, 67.5) * mm, "end": v(-56.15, 48.18) * mm});
            skArc(sketch, "E79.10", {"start": v(-56.15, -48.18) * mm, "mid": v(0, -67.5) * mm, "end": v(56.15, -48.18) * mm});
            skArc(sketch, "E79.11", {"start": v(56.15, -48.18) * mm, "mid": v(58.99, -44.68) * mm, "end": v(60, -40.3) * mm});
            skArc(sketch, "E79.12", {"start": v(-60, -40.3) * mm, "mid": v(-58.99, -44.68) * mm, "end": v(-56.15, -48.18) * mm});
            skLineSegment(sketch, "E79.13", {"start": v(-60, 40.3) * mm, "end": v(-60, -40.3) * mm});
            skArc(sketch, "E79.14", {"start": v(-56.15, 48.18) * mm, "mid": v(-58.99, 44.68) * mm, "end": v(-60, 40.3) * mm});
            skArc(sketch, "E79.15", {"start": v(60, 40.3) * mm, "mid": v(58.99, 44.68) * mm, "end": v(56.15, 48.18) * mm});
            skCircle(sketch, "E79.16", {"center": v(60, 67.5) * mm, "radius": 4 * mm});
            skCircle(sketch, "E79.17", {"center": v(-60, 67.5) * mm, "radius": 4 * mm});
            skCircle(sketch, "E79.18", {"center": v(-60, -67.5) * mm, "radius": 4 * mm});
            skCircle(sketch, "E79.19", {"center": v(60, -67.5) * mm, "radius": 4 * mm});
            skLineSegment(sketch, "E80", {"start": v(-33, 90) * mm, "end": v(-15, 108) * mm});
            skLineSegment(sketch, "E81", {"start": v(-15, 108) * mm, "end": v(-15, 120) * mm});
            skLineSegment(sketch, "E82", {"start": v(33, 90) * mm, "end": v(15, 108) * mm});
            skLineSegment(sketch, "E83", {"start": v(15, 108) * mm, "end": v(15, 120) * mm});
            skArc(sketch, "E84", {"start": v(15, 120) * mm, "mid": v(0, 135) * mm, "end": v(-15, 120) * mm});
            skLineSegment(sketch, "E85", {"start": v(0, 23.75) * mm, "end": v(0, 120) * mm, "construction": true});
            skCircle(sketch, "E86", {"center": v(0, 120) * mm, "radius": 6 * mm});
            skLineSegment(sketch, "E87", {"start": v(-74.25, 0) * mm, "end": v(74.25, 0) * mm, "construction": true});
            skLineSegment(sketch, "E88.MirrorCS", {"start": v(15, -108) * mm, "end": v(15, -120) * mm});
            skLineSegment(sketch, "E89.MirrorCS", {"start": v(33, -90) * mm, "end": v(15, -108) * mm});
            skArc(sketch, "E90.MirrorCS", {"start": v(15, -120) * mm, "mid": v(0, -135) * mm, "end": v(-15, -120) * mm});
            skLineSegment(sketch, "E91.MirrorCS", {"start": v(-15, -108) * mm, "end": v(-15, -120) * mm});
            skLineSegment(sketch, "E92.MirrorCS", {"start": v(-33, -90) * mm, "end": v(-15, -108) * mm});
            skCircle(sketch, "E93.MirrorC", {"center": v(0, -120) * mm, "radius": 6 * mm});
            skLineSegment(sketch, "E94.MirrorCS", {"start": v(0, -23.75) * mm, "end": v(0, -120) * mm, "construction": true});
            skLineSegment(sketch, "E95.trimOffspring", {"start": v(33, -90) * mm, "end": v(70, -90) * mm});
            skLineSegment(sketch, "E96.trimOffspring", {"start": v(33, 90) * mm, "end": v(70, 90) * mm});
            skSolve(sketch);
        }
        {
            var Q0;
            Q0 = qSketchRegion(id + "F16", true);
            var Q1;
            Q1=makeQuery(id+"F2.opExtrude","CAP_FACE",FACE,{"disambiguationData":[OSD([sQuery(id+"F0.wireOp",EDGE,"E12"),sQuery(id+"F0.wireOp",EDGE,"E13"),sQuery(id+"F0.wireOp",EDGE,"E14"),sQuery(id+"F0.wireOp",EDGE,"E15"),sQuery(id+"F0.wireOp",EDGE,"E17.filletArc"),sQuery(id+"F0.wireOp",EDGE,"E18.filletArc"),sQuery(id+"F0.wireOp",EDGE,"E19.filletArc"),sQuery(id+"F0.wireOp",EDGE,"E20.filletArc"),sQuery(id+"F0.wireOp",EDGE,"E25.0"),sQuery(id+"F0.wireOp",EDGE,"E25.1"),sQuery(id+"F0.wireOp",EDGE,"E25.2"),sQuery(id+"F0.wireOp",EDGE,"E25.3"),sQuery(id+"F0.wireOp",EDGE,"E25.4"),sQuery(id+"F0.wireOp",EDGE,"E25.5"),sQuery(id+"F0.wireOp",EDGE,"E25.6"),sQuery(id+"F0.wireOp",EDGE,"E25.7")])],"isStart":false});
            var Q2;
            Q2=makeQuery(id+"F1.opExtrude","SWEPT_BODY",BODY,{"disambiguationData":[OSD([sQuery(id+"F0.wireOp",EDGE,"E1.bottom"),sQuery(id+"F0.wireOp",EDGE,"E1.top"),sQuery(id+"F0.wireOp",EDGE,"E1.left"),sQuery(id+"F0.wireOp",EDGE,"E1.right"),sQuery(id+"F0.wireOp",EDGE,"E4"),sQuery(id+"F0.wireOp",EDGE,"E5"),sQuery(id+"F0.wireOp",EDGE,"E6"),sQuery(id+"F0.wireOp",EDGE,"E7"),sQuery(id+"F0.wireOp",EDGE,"E21.filletArc"),sQuery(id+"F0.wireOp",EDGE,"E22.filletArc"),sQuery(id+"F0.wireOp",EDGE,"E23.filletArc"),sQuery(id+"F0.wireOp",EDGE,"E24.filletArc")])]});
            extrude(context, id + "F17", {"entities" : qUnion([Q0]), "endBound" : BoundingType.UP_TO_SURFACE, "endBoundEntityFace" : qUnion([Q1]), "endBoundEntityBody" : qUnion([Q2]), "depth" : 25 * mm});
        }
    });
